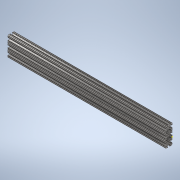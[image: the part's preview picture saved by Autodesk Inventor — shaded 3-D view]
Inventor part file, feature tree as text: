
AUTODESK INVENTOR PART (.ipt)
format: ipt  version: 2020 (Build 240168000, 168)  size: 387,072 bytes
history: native  units: in
note: dims shown in document units (in); Inventor stores cm internally (conversion verified against a paired STEP export)
features: sketch x2, extrude x1
ambient origin geometry x8: Origin, YZ Plane, XZ Plane, XY Plane, X Axis, Y Axis, Z Axis, Center Point
bodies: Solid1 (feature_tree)
feature tree (3):
  extrude  "Extrusion1"  [1 undecoded]
  sketch  "Sketch2"
  sketch  "Sketch1"  dims[d0=24.0in d1=0.0in]
note: 1 required parameter value undecoded (feature->parameter linkage not recoverable at this tier; creation-order binding heuristic only, values carry confidence <= 0.55)
